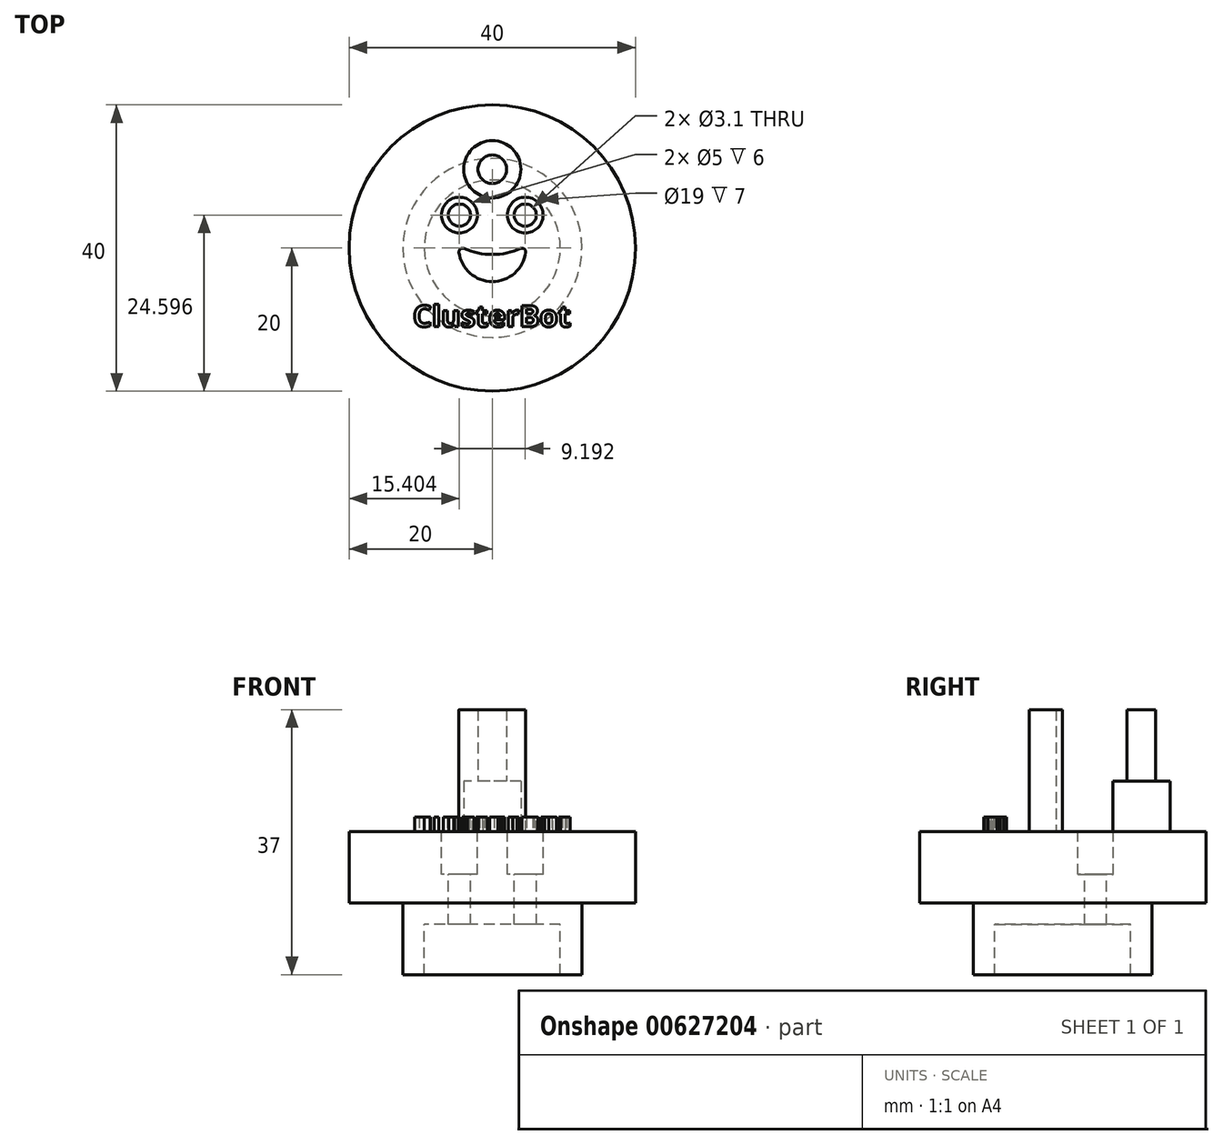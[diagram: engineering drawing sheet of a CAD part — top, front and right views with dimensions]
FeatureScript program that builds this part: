
annotation { "Feature Type Name" : "Feature", "Feature Type Description" : "" }
export const myFeature = defineFeature(function(context is Context, id is Id, definition is map)
    precondition{}
    {
        {
            var Q0;
            Q0=qCreatedBy(makeId("Top.planeOp"),FACE);
            var sketch = newSketch(context, id + "F0", { "sketchPlane" : qUnion([Q0])});
            skCircle(sketch, "E0", {"center": v(0, 0) * mm, "radius": 20 * mm});
            skLineSegment(sketch, "E1", {"start": v(0, 57.86) * mm, "end": v(0, -51.25) * mm, "construction": true});
            skLineSegment(sketch, "E2", {"start": v(-57.98, 0) * mm, "end": v(50.32, 0) * mm, "construction": true});
            skCircle(sketch, "E3", {"center": v(0, 11) * mm, "radius": 2 * mm});
            skCircle(sketch, "E4", {"center": v(0, 0) * mm, "radius": 4.7 * mm});
            skLineSegment(sketch, "E5", {"start": v(0, 11) * mm, "end": v(0, 0) * mm});
            skLineSegment(sketch, "E6", {"start": v(0, 36.77) * mm, "end": v(-4.7, 0.27) * mm, "construction": true});
            skCircle(sketch, "E7", {"center": v(0, 0) * mm, "radius": 9.5 * mm});
            skCircle(sketch, "E8", {"center": v(0, 0) * mm, "radius": 12.5 * mm});
            skArc(sketch, "E9", {"start": v(-4.7, 0.27) * mm, "mid": v(0, -0.9) * mm, "end": v(4.7, 0.27) * mm});
            skSolve(sketch);
        }
        {
            var Q0;
            Q0=makeQuery(id+"F0.imprint","IMPRINT",FACE,{"disambiguationData":[TD([[makeQuery(id+"F0.imprint","IMPRINT",EDGE,{"derivedFrom":sQuery(id+"F0.wireOp",EDGE,"E0")}),1.0]])]});
            var Q1;
            {var subQ0=sQuery(id+"F0.wireOp",EDGE,"EMk8Hpbs-Uu9s-4hnP-Wr23-4mz9YGDRhDCW");var subQ1=sQuery(id+"F0.wireOp",EDGE,"E4");var subQ2=makeQuery(id+"F0.imprint","INTERSECT",VERTEX,{"disambiguationData":[OD(0.0)],"derivedFrom":[subQ1,subQ0]});Q1=makeQuery(id+"F0.imprint","IMPRINT",FACE,{"disambiguationData":[TD([[makeQuery(id+"F0.imprint","IMPRINT",EDGE,{"disambiguationData":[TD([[subQ2,1.0]])],"derivedFrom":subQ1}),1.0]])]});}
            var Q2;
            {var subQ0=sQuery(id+"F0.wireOp",EDGE,"EMk8Hpbs-Uu9s-4hnP-Wr23-4mz9YGDRhDCW");var subQ1=sQuery(id+"F0.wireOp",EDGE,"E4");var subQ2=makeQuery(id+"F0.imprint","INTERSECT",VERTEX,{"disambiguationData":[OD(1.0)],"derivedFrom":[subQ1,subQ0]});Q2=makeQuery(id+"F0.imprint","IMPRINT",FACE,{"disambiguationData":[TD([[makeQuery(id+"F0.imprint","IMPRINT",EDGE,{"disambiguationData":[TD([[subQ2,-1.0]])],"derivedFrom":subQ1}),1.0]])]});}
            var Q3;
            {var subQ3=sQuery(id+"F0.wireOp",EDGE,"E5");var subQ6=sQuery(id+"F0.wireOp",EDGE,"E3");var subQ7=makeQuery(id+"F0.imprint","INTERSECT",VERTEX,{"derivedFrom":[subQ6,subQ3]});Q3=makeQuery(id+"F0.imprint","IMPRINT",FACE,{"disambiguationData":[TD([[makeQuery(id+"F0.imprint","IMPRINT",EDGE,{"disambiguationData":[TD([[subQ7,1.0]])],"derivedFrom":subQ6}),-1.0]])]});}
            extrude(context, id + "F1", {"entities" : qUnion([Q0, Q1, Q2, Q3]), "depth" : 10 * mm, "offsetDistance" : 25 * mm});
        }
        {
            var Q0;
            Q0=makeQuery(id+"F0.imprint","IMPRINT",FACE,{"disambiguationData":[TD([[makeQuery(id+"F0.imprint","IMPRINT",EDGE,{"derivedFrom":sQuery(id+"F0.wireOp",EDGE,"E3")}),1.0]])]});
            var Q1;
            {var subQ0=sQuery(id+"F0.wireOp",EDGE,"EMk8Hpbs-Uu9s-4hnP-Wr23-4mz9YGDRhDCW");var subQ1=sQuery(id+"F0.wireOp",EDGE,"E4");var subQ2=makeQuery(id+"F0.imprint","INTERSECT",VERTEX,{"disambiguationData":[OD(0.0)],"derivedFrom":[subQ1,subQ0]});Q1=makeQuery(id+"F0.imprint","IMPRINT",FACE,{"disambiguationData":[TD([[makeQuery(id+"F0.imprint","IMPRINT",EDGE,{"disambiguationData":[TD([[subQ2,-1.0]])],"derivedFrom":subQ1}),1.0]])]});}
            var Q2;
            {var subQ0=sQuery(id+"F0.wireOp",EDGE,"E8");var subQ1=sQuery(id+"F0.wireOp",EDGE,"E3");var subQ2=makeQuery(id+"F0.imprint","INTERSECT",VERTEX,{"disambiguationData":[OD(0.0)],"derivedFrom":[subQ1,subQ0]});Q2=makeQuery(id+"F0.imprint","IMPRINT",FACE,{"disambiguationData":[TD([[makeQuery(id+"F0.imprint","IMPRINT",EDGE,{"disambiguationData":[TD([[subQ2,1.0]])],"derivedFrom":subQ1}),1.0]])]});}
            var Q3;
            {var subQ0=sQuery(id+"F0.wireOp",EDGE,"E5");var subQ1=sQuery(id+"F0.wireOp",EDGE,"E3");var subQ2=makeQuery(id+"F0.imprint","INTERSECT",VERTEX,{"derivedFrom":[subQ1,subQ0]});Q3=makeQuery(id+"F0.imprint","IMPRINT",FACE,{"disambiguationData":[TD([[makeQuery(id+"F0.imprint","IMPRINT",EDGE,{"disambiguationData":[TD([[subQ2,-1.0]])],"derivedFrom":subQ1}),1.0]])]});}
            var Q4;
            {var subQ0=sQuery(id+"F0.wireOp",EDGE,"E5");var subQ1=sQuery(id+"F0.wireOp",EDGE,"E3");var subQ2=makeQuery(id+"F0.imprint","INTERSECT",VERTEX,{"derivedFrom":[subQ1,subQ0]});Q4=makeQuery(id+"F0.imprint","IMPRINT",FACE,{"disambiguationData":[TD([[makeQuery(id+"F0.imprint","IMPRINT",EDGE,{"disambiguationData":[TD([[subQ2,1.0]])],"derivedFrom":subQ1}),1.0]])]});}
            extrude(context, id + "F2", {"entities" : qUnion([Q0, Q1, Q2, Q3, Q4]), "operationType" : NewBodyOperationType.ADD, "depth" : 27 * mm, "offsetDistance" : 25 * mm});
        }
        {
            var Q0;
            {var subQ0=sQuery(id+"F0.wireOp",EDGE,"E8");var subQ1=sQuery(id+"F0.wireOp",EDGE,"E3");var subQ2=makeQuery(id+"F0.imprint","INTERSECT",VERTEX,{"disambiguationData":[OD(0.0)],"derivedFrom":[subQ1,subQ0]});Q0=makeQuery(id+"F0.imprint","IMPRINT",FACE,{"disambiguationData":[TD([[makeQuery(id+"F0.imprint","IMPRINT",EDGE,{"disambiguationData":[TD([[subQ2,-1.0]])],"derivedFrom":subQ1}),-1.0]])]});}
            extrude(context, id + "F3", {"entities" : qUnion([Q0]), "operationType" : NewBodyOperationType.ADD, "oppositeDirection" : true, "depth" : 10 * mm, "offsetDistance" : 25 * mm, "hasSecondDirection" : true, "secondDirectionOppositeDirection" : false, "secondDirectionDepth" : 10 * mm});
        }
        {
            var Q0;
            {var subQ2=sQuery(id+"F0.wireOp",EDGE,"E3");var subQ5=sQuery(id+"F0.wireOp",EDGE,"E8");var subQ6=makeQuery(id+"F0.imprint","INTERSECT",VERTEX,{"disambiguationData":[OD(0.0)],"derivedFrom":[subQ2,subQ5]});Q0=makeQuery(id+"F0.imprint","IMPRINT",FACE,{"disambiguationData":[TD([[makeQuery(id+"F0.imprint","IMPRINT",EDGE,{"disambiguationData":[TD([[subQ6,-1.0]])],"derivedFrom":subQ2}),1.0]])]});}
            extrude(context, id + "F4", {"entities" : qUnion([Q0]), "operationType" : NewBodyOperationType.ADD, "oppositeDirection" : true, "depth" : 10 * mm, "offsetDistance" : 25 * mm});
        }
        {
            var Q0;
            {var subQ0=sQuery(id+"F0.wireOp",EDGE,"E9");var subQ1=sQuery(id+"F0.wireOp",EDGE,"E4");Q0=makeQuery(id+"F2.opExtrude","SWEPT_EDGE",EDGE,{"disambiguationData":[OSD([subQ1,subQ0]),TDD([makeQuery(id+"F0.imprint","INTERSECT",VERTEX,{"disambiguationData":[OD(1.0)],"derivedFrom":[subQ1,subQ0]})])]});}
            var Q1;
            {var subQ0=sQuery(id+"F0.wireOp",EDGE,"E9");var subQ1=sQuery(id+"F0.wireOp",EDGE,"E4");Q1=makeQuery(id+"F2.opExtrude","SWEPT_EDGE",EDGE,{"disambiguationData":[OSD([subQ1,subQ0]),TDD([makeQuery(id+"F0.imprint","INTERSECT",VERTEX,{"disambiguationData":[OD(0.0)],"derivedFrom":[subQ1,subQ0]})])]});}
            fillet(context, id + "F5", {"entities" : qUnion([Q0, Q1]), "radius" : 0.5 * mm, "tangentPropagation" : true, "allowEdgeOverflow" : false});
        }
        {
            var Q0;
            {var subQ0=sQuery(id+"F0.wireOp",EDGE,"E8");var subQ1=sQuery(id+"F0.wireOp",EDGE,"E7");var subQ2=sQuery(id+"F0.wireOp",EDGE,"E3");Q0=makeQuery(id+"F3.boolean.opBoolean","MERGE",FACE,{"derivedFrom":[makeQuery(id+"F1.opExtrude","CAP_FACE",FACE,{"disambiguationData":[OSD([sQuery(id+"F0.wireOp",EDGE,"E0"),subQ2,subQ0])],"isStart":false}),makeQuery(id+"F1.opExtrude","CAP_FACE",FACE,{"disambiguationData":[OSD([subQ2,sQuery(id+"F0.wireOp",EDGE,"E4"),subQ1,sQuery(id+"F0.wireOp",EDGE,"E9")])],"isStart":false}),makeQuery(id+"F3.opExtrude","CAP_FACE",FACE,{"disambiguationData":[OSD([subQ2,subQ1,subQ0])],"isStart":true})]});}
            var sketch = newSketch(context, id + "F6", { "sketchPlane" : qUnion([Q0])});
            skLineSegment(sketch, "E10", {"start": v(0, 0) * mm, "end": v(-10.6, 10.6) * mm, "construction": true});
            skLineSegment(sketch, "E11", {"start": v(0, 0) * mm, "end": v(10.6, 10.6) * mm, "construction": true});
            skCircle(sketch, "E12", {"center": v(4.6, 4.6) * mm, "radius": 1.55 * mm});
            skCircle(sketch, "E13", {"center": v(4.6, 4.6) * mm, "radius": 2.5 * mm});
            skCircle(sketch, "E14", {"center": v(-4.6, 4.6) * mm, "radius": 1.55 * mm});
            skCircle(sketch, "E15", {"center": v(-4.6, 4.6) * mm, "radius": 2.5 * mm});
            skSolve(sketch);
        }
        {
            var Q0;
            Q0=makeQuery(id+"F6.imprint","IMPRINT",FACE,{"disambiguationData":[TD([[makeQuery(id+"F6.imprint","IMPRINT",EDGE,{"derivedFrom":sQuery(id+"F6.wireOp",EDGE,"E14")}),1.0]])]});
            var Q1;
            Q1=makeQuery(id+"F6.imprint","IMPRINT",FACE,{"disambiguationData":[TD([[makeQuery(id+"F6.imprint","IMPRINT",EDGE,{"derivedFrom":sQuery(id+"F6.wireOp",EDGE,"E12")}),1.0]])]});
            extrude(context, id + "F7", {"entities" : qUnion([Q0, Q1]), "operationType" : NewBodyOperationType.REMOVE, "oppositeDirection" : true, "depth" : 10 * mm, "offsetDistance" : 25 * mm});
        }
        {
            var Q0;
            Q0=makeQuery(id+"F6.imprint","IMPRINT",FACE,{"disambiguationData":[TD([[makeQuery(id+"F6.imprint","IMPRINT",EDGE,{"derivedFrom":sQuery(id+"F6.wireOp",EDGE,"E12")}),-1.0]])]});
            var Q1;
            Q1=makeQuery(id+"F6.imprint","IMPRINT",FACE,{"disambiguationData":[TD([[makeQuery(id+"F6.imprint","IMPRINT",EDGE,{"derivedFrom":sQuery(id+"F6.wireOp",EDGE,"E14")}),-1.0]])]});
            extrude(context, id + "F8", {"entities" : qUnion([Q0, Q1]), "operationType" : NewBodyOperationType.REMOVE, "oppositeDirection" : true, "depth" : 6 * mm, "offsetDistance" : 25 * mm});
        }
        {
            var Q0;
            {var subQ0=sQuery(id+"F0.wireOp",EDGE,"E8");var subQ1=sQuery(id+"F0.wireOp",EDGE,"E7");var subQ2=sQuery(id+"F0.wireOp",EDGE,"E3");Q0=makeQuery(id+"F3.boolean.opBoolean","MERGE",FACE,{"derivedFrom":[makeQuery(id+"F1.opExtrude","CAP_FACE",FACE,{"disambiguationData":[OSD([sQuery(id+"F0.wireOp",EDGE,"E0"),subQ2,subQ0])],"isStart":false}),makeQuery(id+"F1.opExtrude","CAP_FACE",FACE,{"disambiguationData":[OSD([subQ2,sQuery(id+"F0.wireOp",EDGE,"E4"),subQ1,sQuery(id+"F0.wireOp",EDGE,"E9")])],"isStart":false}),makeQuery(id+"F3.opExtrude","CAP_FACE",FACE,{"disambiguationData":[OSD([subQ2,subQ1,subQ0])],"isStart":true})]});}
            var sketch = newSketch(context, id + "F9", { "sketchPlane" : qUnion([Q0])});
            skText(sketch, "E16", { "text": "ClusterBot", "fontName": "OpenSans-Bold.ttf"});
            const initialGuessF9  = {"E16": [-0.01111, -0.011, 1, 0, 0.003]};
            skSetInitialGuess(sketch, initialGuessF9);
            skSolve(sketch);
        }
        {
            var Q0;
            Q0 = qSketchRegion(id + "F9", true);
            extrude(context, id + "F10", {"entities" : qUnion([Q0]), "operationType" : NewBodyOperationType.ADD, "depth" : 2 * mm, "offsetDistance" : 25 * mm});
        }
        {
            var Q0;
            {var subQ0=sQuery(id+"F0.wireOp",EDGE,"E9");var subQ1=sQuery(id+"F0.wireOp",EDGE,"E4");var subQ2=sQuery(id+"F0.wireOp",EDGE,"E3");var subQ3=sQuery(id+"F0.wireOp",EDGE,"E0");var subQ4=sQuery(id+"F0.wireOp",EDGE,"E8");var subQ5=sQuery(id+"F0.wireOp",EDGE,"E7");Q0=makeQuery(id+"F10.boolean.opBoolean","SPLIT",FACE,{"disambiguationData":[TD([makeQuery(id+"F1.opExtrude","SWEPT_FACE",FACE,{"disambiguationData":[OSD([subQ3])]})])],"derivedFrom":makeQuery(id+"F3.boolean.opBoolean","MERGE",FACE,{"derivedFrom":[makeQuery(id+"F1.opExtrude","CAP_FACE",FACE,{"disambiguationData":[OSD([subQ3,subQ2,subQ4])],"isStart":false}),makeQuery(id+"F1.opExtrude","CAP_FACE",FACE,{"disambiguationData":[OSD([subQ2,subQ1,subQ5,subQ0])],"isStart":false}),makeQuery(id+"F3.opExtrude","CAP_FACE",FACE,{"disambiguationData":[OSD([subQ2,subQ5,subQ4])],"isStart":true})]})});}
            var sketch = newSketch(context, id + "F11", { "sketchPlane" : qUnion([Q0])});
            skCircle(sketch, "E17", {"center": v(0, 11) * mm, "radius": 4 * mm});
            skSolve(sketch);
        }
        {
            var Q0;
            Q0 = qSketchRegion(id + "F11", true);
            extrude(context, id + "F12", {"entities" : qUnion([Q0]), "operationType" : NewBodyOperationType.ADD, "depth" : 7 * mm, "offsetDistance" : 25 * mm});
        }
        {
            var Q0;
            {var subQ0=sQuery(id+"F0.wireOp",EDGE,"E7");var subQ1=sQuery(id+"F0.wireOp",EDGE,"E9");var subQ2=sQuery(id+"F0.wireOp",EDGE,"E4");var subQ3=sQuery(id+"F0.wireOp",EDGE,"E3");Q0=makeQuery(id+"F4.boolean.opBoolean","SPLIT",FACE,{"disambiguationData":[TD([makeQuery(id+"F3.opExtrude","SWEPT_FACE",FACE,{"disambiguationData":[OSD([subQ0])]})])],"derivedFrom":makeQuery(id+"F2.boolean.opBoolean","MERGE",FACE,{"derivedFrom":[makeQuery(id+"F1.opExtrude","CAP_FACE",FACE,{"disambiguationData":[OSD([sQuery(id+"F0.wireOp",EDGE,"E0"),subQ3,sQuery(id+"F0.wireOp",EDGE,"E8")])],"isStart":true}),makeQuery(id+"F1.opExtrude","CAP_FACE",FACE,{"disambiguationData":[OSD([subQ3,subQ2,subQ0,subQ1])],"isStart":true}),makeQuery(id+"F2.opExtrude","CAP_FACE",FACE,{"disambiguationData":[OSD([subQ3])],"isStart":true}),makeQuery(id+"F2.opExtrude","CAP_FACE",FACE,{"disambiguationData":[OSD([subQ2,subQ1])],"isStart":true})]})});}
            extrude(context, id + "F13", {"entities" : qUnion([Q0]), "operationType" : NewBodyOperationType.ADD, "depth" : 3 * mm, "offsetDistance" : 25 * mm});
        }
    });
